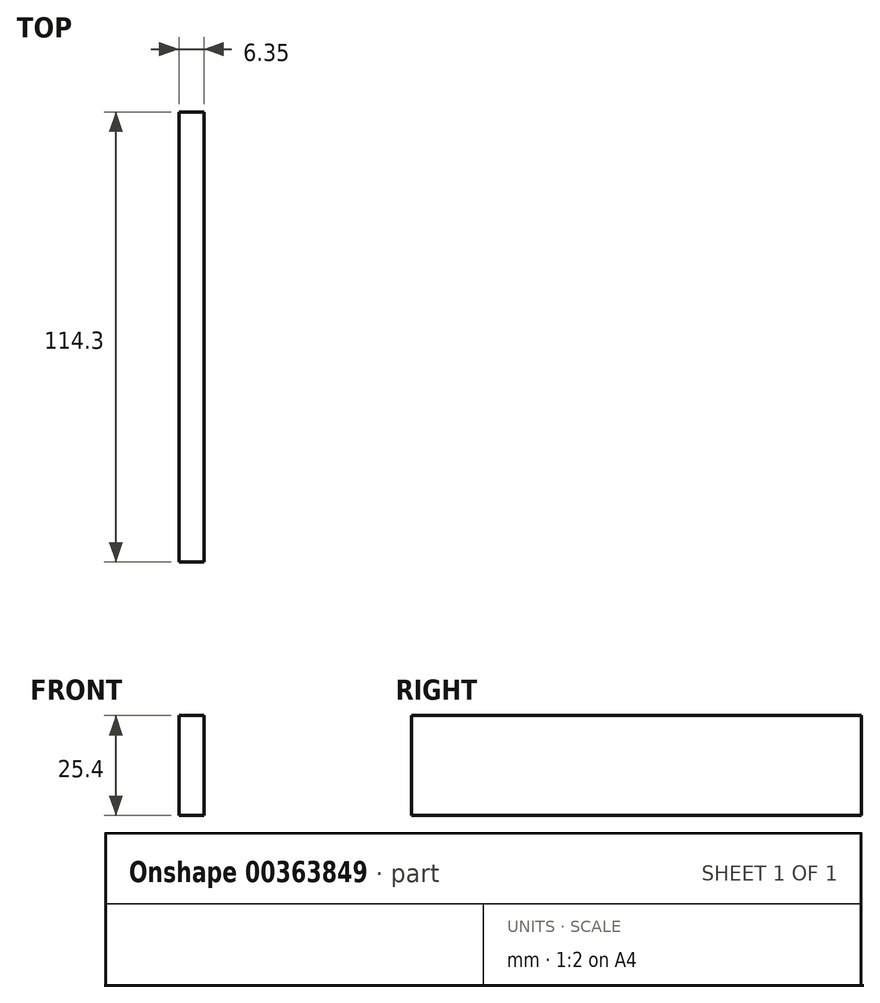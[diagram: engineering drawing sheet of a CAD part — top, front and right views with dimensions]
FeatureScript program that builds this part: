
annotation { "Feature Type Name" : "Feature", "Feature Type Description" : "" }
export const myFeature = defineFeature(function(context is Context, id is Id, definition is map)
    precondition{}
    {
        {
            var Q0;
            Q0=qCreatedBy(makeId("Right.planeOp"),FACE);
            var sketch = newSketch(context, id + "F0", { "sketchPlane" : qUnion([Q0])});
            skLineSegment(sketch, "E0.bottom", {"start": v(-87.66, -36.02) * mm, "end": v(26.64, -36.02) * mm});
            skLineSegment(sketch, "E0.top", {"start": v(-87.66, -61.42) * mm, "end": v(26.64, -61.42) * mm});
            skLineSegment(sketch, "E0.left", {"start": v(-87.66, -36.02) * mm, "end": v(-87.66, -61.42) * mm});
            skLineSegment(sketch, "E0.right", {"start": v(26.64, -36.02) * mm, "end": v(26.64, -61.42) * mm});
            skSolve(sketch);
        }
        {
            var Q0;
            Q0 = qSketchRegion(id + "F0", true);
            extrude(context, id + "F1", {"entities" : qUnion([Q0]), "depth" : 6.35 * mm});
        }
    });
